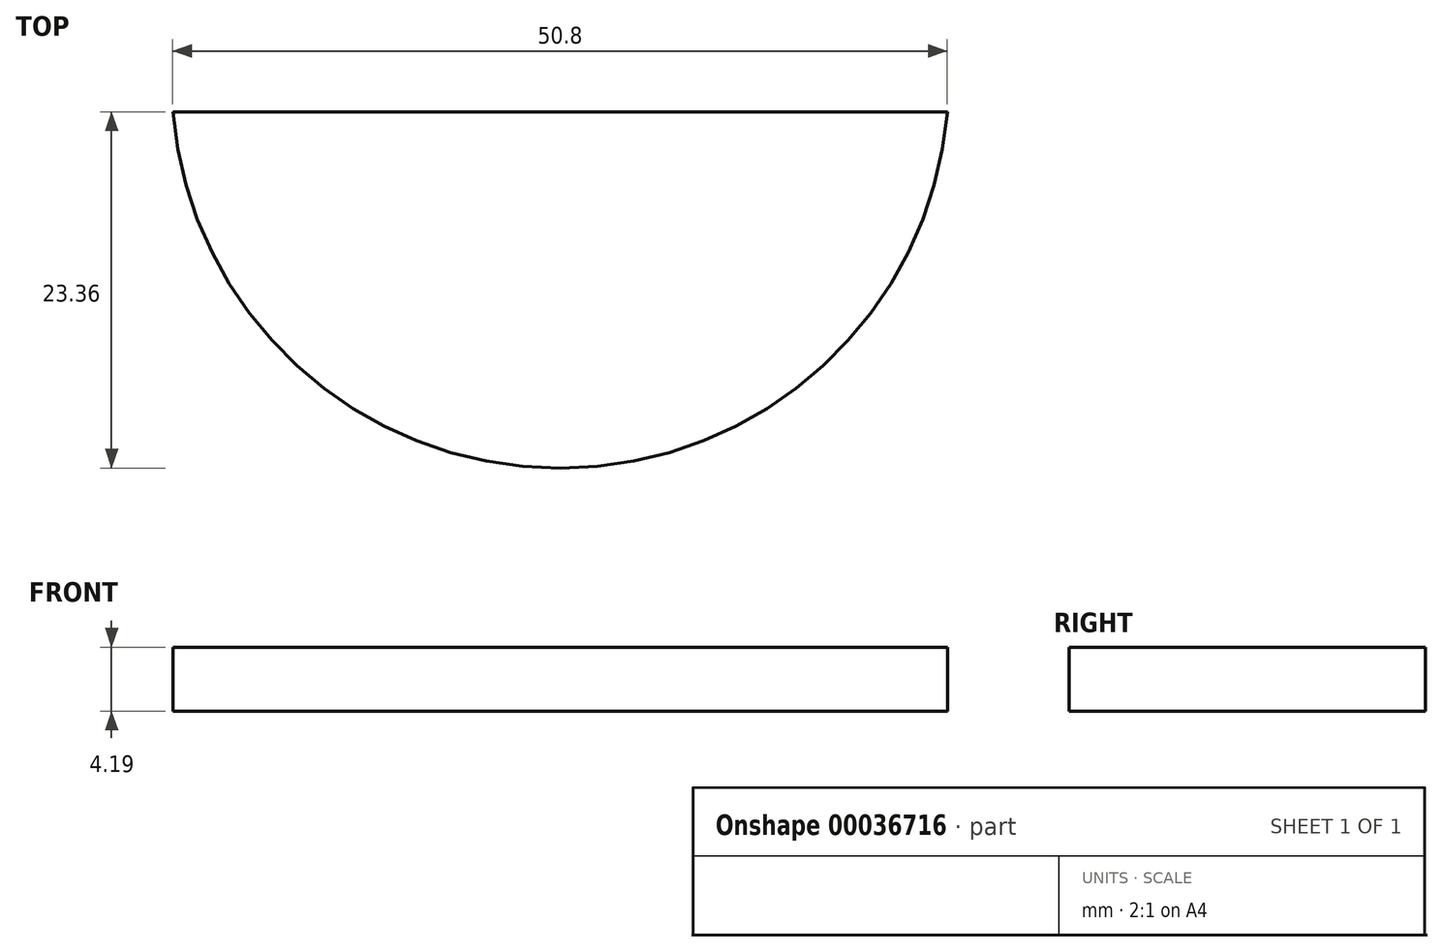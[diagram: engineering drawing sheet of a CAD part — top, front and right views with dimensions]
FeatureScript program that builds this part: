
annotation { "Feature Type Name" : "Feature", "Feature Type Description" : "" }
export const myFeature = defineFeature(function(context is Context, id is Id, definition is map)
    precondition{}
    {
        {
            var Q0;
            Q0=qCreatedBy(makeId("Top.planeOp"),FACE);
            var sketch = newSketch(context, id + "F0", { "sketchPlane" : qUnion([Q0])});
            skArc(sketch, "E0", {"start": v(-27.67, 0) * mm, "mid": v(-2.27, -23.36) * mm, "end": v(23.13, 0) * mm});
            skLineSegment(sketch, "E1", {"start": v(-27.67, 0) * mm, "end": v(23.13, 0) * mm});
            skLineSegment(sketch, "E2", {"start": v(23.13, 0) * mm, "end": v(18.94, 0) * mm});
            skLineSegment(sketch, "E3", {"start": v(5.78, 0) * mm, "end": v(9.97, 0) * mm});
            skLineSegment(sketch, "E4", {"start": v(-10.27, 0) * mm, "end": v(-6.08, 0) * mm});
            skLineSegment(sketch, "E5", {"start": v(-27.67, 0) * mm, "end": v(-23.47, 0) * mm});
            skSolve(sketch);
        }
        {
            var Q0;
            Q0 = qSketchRegion(id + "F0", true);
            extrude(context, id + "F1", {"entities" : qUnion([Q0]), "depth" : 4.2 * mm});
        }
    });
